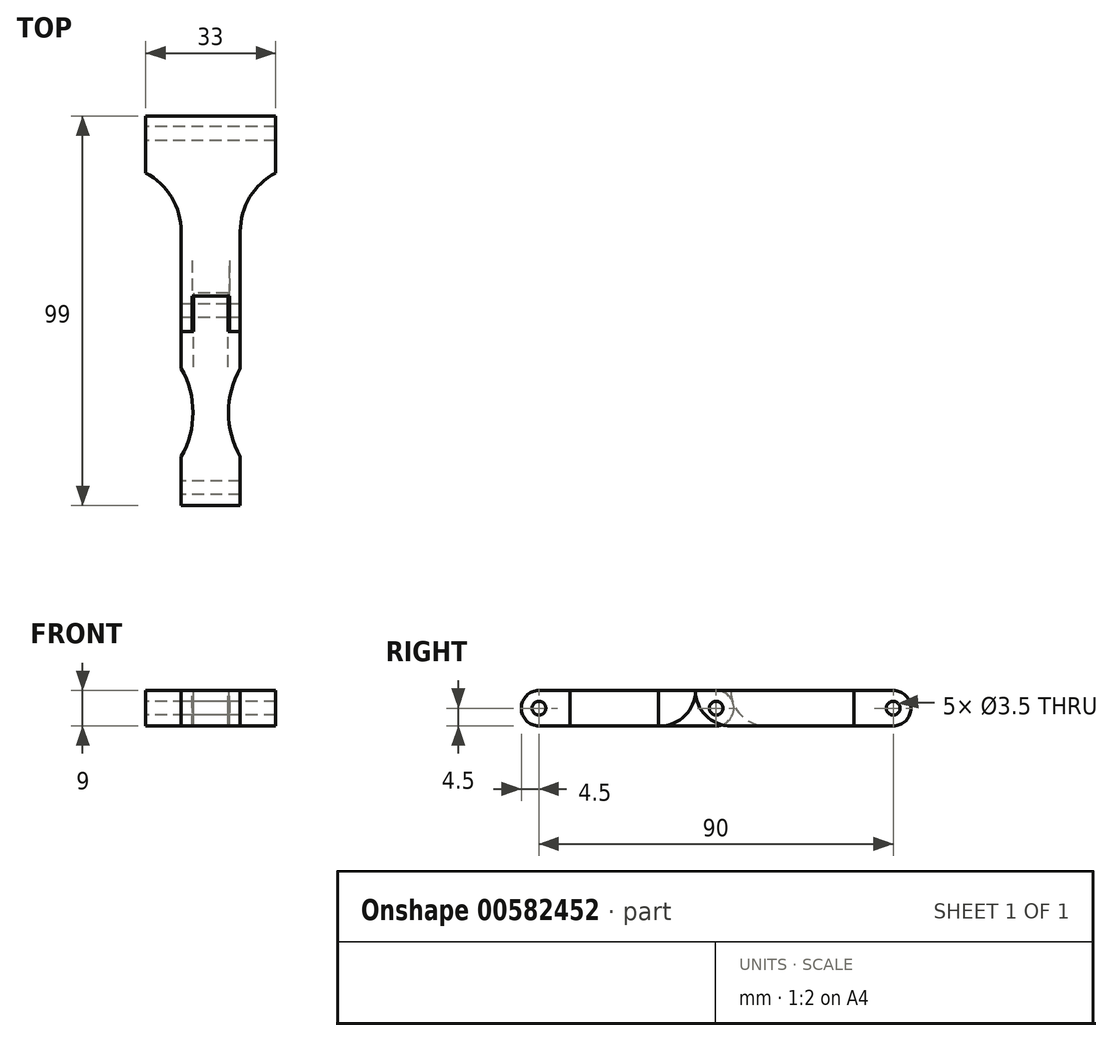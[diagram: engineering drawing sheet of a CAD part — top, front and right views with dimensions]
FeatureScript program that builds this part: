
annotation { "Feature Type Name" : "Feature", "Feature Type Description" : "" }
export const myFeature = defineFeature(function(context is Context, id is Id, definition is map)
    precondition{}
    {
        {
            var Q0;
            Q0=qCreatedBy(makeId("Right.planeOp"),FACE);
            var sketch = newSketch(context, id + "F0", { "sketchPlane" : qUnion([Q0])});
            skLineSegment(sketch, "E0", {"start": v(-22.5, 0) * mm, "end": v(8.25, 0) * mm});
            skLineSegment(sketch, "E1", {"start": v(-22.5, 9) * mm, "end": v(17.25, 9) * mm});
            skArc(sketch, "E2", {"start": v(-22.5, 9) * mm, "mid": v(-27, 4.5) * mm, "end": v(-22.5, 0) * mm});
            skArc(sketch, "E3", {"start": v(8.25, 0) * mm, "mid": v(14.61, 2.64) * mm, "end": v(17.25, 9) * mm});
            skSolve(sketch);
        }
        {
            var Q0;
            Q0 = qSketchRegion(id + "F0", true);
            extrude(context, id + "F1", {"entities" : qUnion([Q0]), "endBound" : BoundingType.SYMMETRIC, "oppositeDirection" : true, "depth" : 15 * mm, "offsetDistance" : 25 * mm});
        }
        {
            var Q0;
            Q0=qCreatedBy(makeId("Right.planeOp"),FACE);
            var sketch = newSketch(context, id + "F2", { "sketchPlane" : qUnion([Q0])});
            skLineSegment(sketch, "E4", {"start": v(0, 9) * mm, "end": v(0, 0) * mm});
            skLineSegment(sketch, "E5", {"start": v(0, 0) * mm, "end": v(22.5, 0) * mm});
            skLineSegment(sketch, "E6", {"start": v(0, 9) * mm, "end": v(22.5, 9) * mm});
            skArc(sketch, "E7", {"start": v(22.5, 0) * mm, "mid": v(27, 4.5) * mm, "end": v(22.5, 9) * mm});
            skSolve(sketch);
        }
        {
            var Q0;
            Q0 = qSketchRegion(id + "F2", true);
            extrude(context, id + "F3", {"entities" : qUnion([Q0]), "operationType" : NewBodyOperationType.ADD, "endBound" : BoundingType.SYMMETRIC, "depth" : 8.8 * mm, "offsetDistance" : 25 * mm});
        }
        {
            var Q0;
            Q0=qCreatedBy(makeId("Top.planeOp"),FACE);
            var sketch = newSketch(context, id + "F4", { "sketchPlane" : qUnion([Q0])});
            skCircle(sketch, "E8", {"center": v(-27, -3.37) * mm, "radius": 22.5 * mm});
            skSolve(sketch);
        }
        {
            var Q0;
            Q0 = qSketchRegion(id + "F4", true);
            extrude(context, id + "F5", {"entities" : qUnion([Q0]), "depth" : 25 * mm, "offsetDistance" : 25 * mm});
        }
        {
            var Q0;
            Q0=makeQuery(id+"F5.opExtrude","SWEPT_BODY",BODY,{"disambiguationData":[OSD([sQuery(id+"F4.wireOp",EDGE,"E8")])]});
            var Q1;
            Q1=qCreatedBy(makeId("Right.planeOp"),FACE);
            mirror(context, id + "F6", {"entities" : qUnion([Q0]), "mirrorPlane" : qUnion([Q1])});
        }
        {
            var Q0;
            Q0=makeQuery(id+"F6.opPattern","COPY",BODY,{"derivedFrom":makeQuery(id+"F5.opExtrude","SWEPT_BODY",BODY,{"disambiguationData":[OSD([sQuery(id+"F4.wireOp",EDGE,"E8")])]}),"instanceName":"1"});
            var Q1;
            Q1=makeQuery(id+"F5.opExtrude","SWEPT_BODY",BODY,{"disambiguationData":[OSD([sQuery(id+"F4.wireOp",EDGE,"E8")])]});
            var Q2;
            Q2=makeQuery(id+"F1.opExtrude","SWEPT_BODY",BODY,{"disambiguationData":[OSD([sQuery(id+"F0.wireOp",EDGE,"E0"),sQuery(id+"F0.wireOp",EDGE,"E1"),sQuery(id+"F0.wireOp",EDGE,"E2"),sQuery(id+"F0.wireOp",EDGE,"E3")])]});
            booleanBodies(context, id + "F7", {"operationType" : BooleanOperationType.SUBTRACTION, "tools" : qUnion([Q0, Q1]), "targets" : qUnion([Q2])});
        }
        {
            var Q0;
            Q0=qCreatedBy(makeId("Right.planeOp"),FACE);
            var sketch = newSketch(context, id + "F8", { "sketchPlane" : qUnion([Q0])});
            skLineSegment(sketch, "E9", {"start": v(17.25, 9) * mm, "end": v(67.5, 9) * mm});
            skLineSegment(sketch, "E10", {"start": v(26.25, 0) * mm, "end": v(67.5, 0) * mm});
            skArc(sketch, "E11", {"start": v(17.25, 9) * mm, "mid": v(19.89, 2.64) * mm, "end": v(26.25, 0) * mm});
            skArc(sketch, "E12", {"start": v(67.5, 0) * mm, "mid": v(72, 4.5) * mm, "end": v(67.5, 9) * mm});
            skSolve(sketch);
        }
        {
            var Q0;
            Q0 = qSketchRegion(id + "F8", true);
            extrude(context, id + "F9", {"entities" : qUnion([Q0]), "endBound" : BoundingType.SYMMETRIC, "depth" : 33 * mm, "offsetDistance" : 25 * mm});
        }
        {
            var Q0;
            Q0=qCreatedBy(makeId("Top.planeOp"),FACE);
            var sketch = newSketch(context, id + "F10", { "sketchPlane" : qUnion([Q0])});
            skLineSegment(sketch, "E13", {"start": v(7.5, 16.5) * mm, "end": v(7.5, 42.6) * mm});
            skLineSegment(sketch, "E14", {"start": v(7.5, 16.5) * mm, "end": v(18.75, 16.5) * mm});
            skLineSegment(sketch, "E15", {"start": v(18.75, 16.5) * mm, "end": v(18.75, 58.5) * mm});
            skArc(sketch, "E16", {"start": v(18.75, 58.5) * mm, "mid": v(10.6, 52.34) * mm, "end": v(7.5, 42.6) * mm});
            skSolve(sketch);
        }
        {
            var Q0;
            Q0 = qSketchRegion(id + "F10", true);
            extrude(context, id + "F11", {"entities" : qUnion([Q0]), "depth" : 25 * mm, "offsetDistance" : 25 * mm});
        }
        {
            var Q0;
            Q0=makeQuery(id+"F11.opExtrude","SWEPT_BODY",BODY,{"disambiguationData":[OSD([sQuery(id+"F10.wireOp",EDGE,"E13"),sQuery(id+"F10.wireOp",EDGE,"E14"),sQuery(id+"F10.wireOp",EDGE,"E15"),sQuery(id+"F10.wireOp",EDGE,"E16")])]});
            var Q1;
            Q1=qCreatedBy(makeId("Right.planeOp"),FACE);
            mirror(context, id + "F12", {"entities" : qUnion([Q0]), "mirrorPlane" : qUnion([Q1])});
        }
        {
            var Q0;
            Q0=qCreatedBy(makeId("Top.planeOp"),FACE);
            var sketch = newSketch(context, id + "F13", { "sketchPlane" : qUnion([Q0])});
            skLineSegment(sketch, "E17.bottom", {"start": v(-4.75, 15) * mm, "end": v(4.75, 15) * mm});
            skLineSegment(sketch, "E17.top", {"start": v(-4.75, 26.25) * mm, "end": v(4.75, 26.25) * mm});
            skLineSegment(sketch, "E17.left", {"start": v(-4.75, 15) * mm, "end": v(-4.75, 26.25) * mm});
            skLineSegment(sketch, "E17.right", {"start": v(4.75, 15) * mm, "end": v(4.75, 26.25) * mm});
            skSolve(sketch);
        }
        {
            var Q0;
            Q0 = qSketchRegion(id + "F13", true);
            extrude(context, id + "F14", {"entities" : qUnion([Q0]), "depth" : 25 * mm, "offsetDistance" : 25 * mm});
        }
        {
            var Q0;
            Q0=makeQuery(id+"F12.opPattern","COPY",BODY,{"derivedFrom":makeQuery(id+"F11.opExtrude","SWEPT_BODY",BODY,{"disambiguationData":[OSD([sQuery(id+"F10.wireOp",EDGE,"E13"),sQuery(id+"F10.wireOp",EDGE,"E14"),sQuery(id+"F10.wireOp",EDGE,"E15"),sQuery(id+"F10.wireOp",EDGE,"E16")])]}),"instanceName":"1"});
            var Q1;
            Q1=makeQuery(id+"F11.opExtrude","SWEPT_BODY",BODY,{"disambiguationData":[OSD([sQuery(id+"F10.wireOp",EDGE,"E13"),sQuery(id+"F10.wireOp",EDGE,"E14"),sQuery(id+"F10.wireOp",EDGE,"E15"),sQuery(id+"F10.wireOp",EDGE,"E16")])]});
            var Q2;
            Q2=makeQuery(id+"F14.opExtrude","SWEPT_BODY",BODY,{"disambiguationData":[OSD([sQuery(id+"F13.wireOp",EDGE,"E17.bottom"),sQuery(id+"F13.wireOp",EDGE,"E17.top"),sQuery(id+"F13.wireOp",EDGE,"E17.left"),sQuery(id+"F13.wireOp",EDGE,"E17.right")])]});
            var Q3;
            Q3=makeQuery(id+"F9.opExtrude","SWEPT_BODY",BODY,{"disambiguationData":[OSD([sQuery(id+"F8.wireOp",EDGE,"E9"),sQuery(id+"F8.wireOp",EDGE,"E10"),sQuery(id+"F8.wireOp",EDGE,"E11"),sQuery(id+"F8.wireOp",EDGE,"E12")])]});
            booleanBodies(context, id + "F15", {"operationType" : BooleanOperationType.SUBTRACTION, "tools" : qUnion([Q0, Q1, Q2]), "targets" : qUnion([Q3])});
        }
        {
            var Q0;
            Q0=makeQuery(id+"F15.opBoolean","MERGE",EDGE,{"derivedFrom":[makeQuery(id+"F9.opExtrude","SWEPT_EDGE",EDGE,{"disambiguationData":[OSD([sQuery(id+"F8.wireOp",EDGE,"E10"),sQuery(id+"F8.wireOp",EDGE,"E11")])]}),makeQuery(id+"F14.opExtrude","CAP_EDGE",EDGE,{"disambiguationData":[OSD([sQuery(id+"F13.wireOp",EDGE,"E17.top")])],"isStart":true})]});
            fillet(context, id + "F16", {"entities" : qUnion([Q0]), "radius" : 9 * mm, "tangentPropagation" : true, "allowEdgeOverflow" : false});
        }
        {
            var Q0;
            Q0=makeQuery(id+"F1.opExtrude","CAP_FACE",FACE,{"disambiguationData":[OSD([sQuery(id+"F0.wireOp",EDGE,"E0"),sQuery(id+"F0.wireOp",EDGE,"E1"),sQuery(id+"F0.wireOp",EDGE,"E2"),sQuery(id+"F0.wireOp",EDGE,"Y4NXCHzA-bI5U-HKo0-KCwS-FosxN2STG4DC")])],"isStart":true});
            var sketch = newSketch(context, id + "F17", { "sketchPlane" : qUnion([Q0])});
            skCircle(sketch, "E18", {"center": v(-22.5, 4.5) * mm, "radius": 1.75 * mm});
            skCircle(sketch, "E19", {"center": v(22.5, 4.5) * mm, "radius": 1.75 * mm});
            skCircle(sketch, "E20", {"center": v(67.5, 4.5) * mm, "radius": 1.75 * mm});
            skSolve(sketch);
        }
        {
            var Q0;
            Q0 = qSketchRegion(id + "F17", true);
            extrude(context, id + "F18", {"entities" : qUnion([Q0]), "endBound" : BoundingType.SYMMETRIC, "depth" : 80 * mm, "offsetDistance" : 25 * mm});
        }
        {
            var Q0;
            Q0=makeQuery(id+"F18.opExtrude","SWEPT_BODY",BODY,{"disambiguationData":[OSD([sQuery(id+"F17.wireOp",EDGE,"E19")])]});
            var Q1;
            Q1=makeQuery(id+"F18.opExtrude","SWEPT_BODY",BODY,{"disambiguationData":[OSD([sQuery(id+"F17.wireOp",EDGE,"E18")])]});
            var Q2;
            Q2=makeQuery(id+"F18.opExtrude","SWEPT_BODY",BODY,{"disambiguationData":[OSD([sQuery(id+"F17.wireOp",EDGE,"E20")])]});
            var Q3;
            Q3=makeQuery(id+"F1.opExtrude","SWEPT_BODY",BODY,{"disambiguationData":[OSD([sQuery(id+"F0.wireOp",EDGE,"E0"),sQuery(id+"F0.wireOp",EDGE,"E1"),sQuery(id+"F0.wireOp",EDGE,"E2"),sQuery(id+"F0.wireOp",EDGE,"Y4NXCHzA-bI5U-HKo0-KCwS-FosxN2STG4DC")])]});
            var Q4;
            Q4=makeQuery(id+"F9.opExtrude","SWEPT_BODY",BODY,{"disambiguationData":[OSD([sQuery(id+"F8.wireOp",EDGE,"E9"),sQuery(id+"F8.wireOp",EDGE,"E10"),sQuery(id+"F8.wireOp",EDGE,"E11"),sQuery(id+"F8.wireOp",EDGE,"E12")])]});
            booleanBodies(context, id + "F19", {"operationType" : BooleanOperationType.SUBTRACTION, "tools" : qUnion([Q0, Q1, Q2]), "targets" : qUnion([Q3, Q4])});
        }
    });
